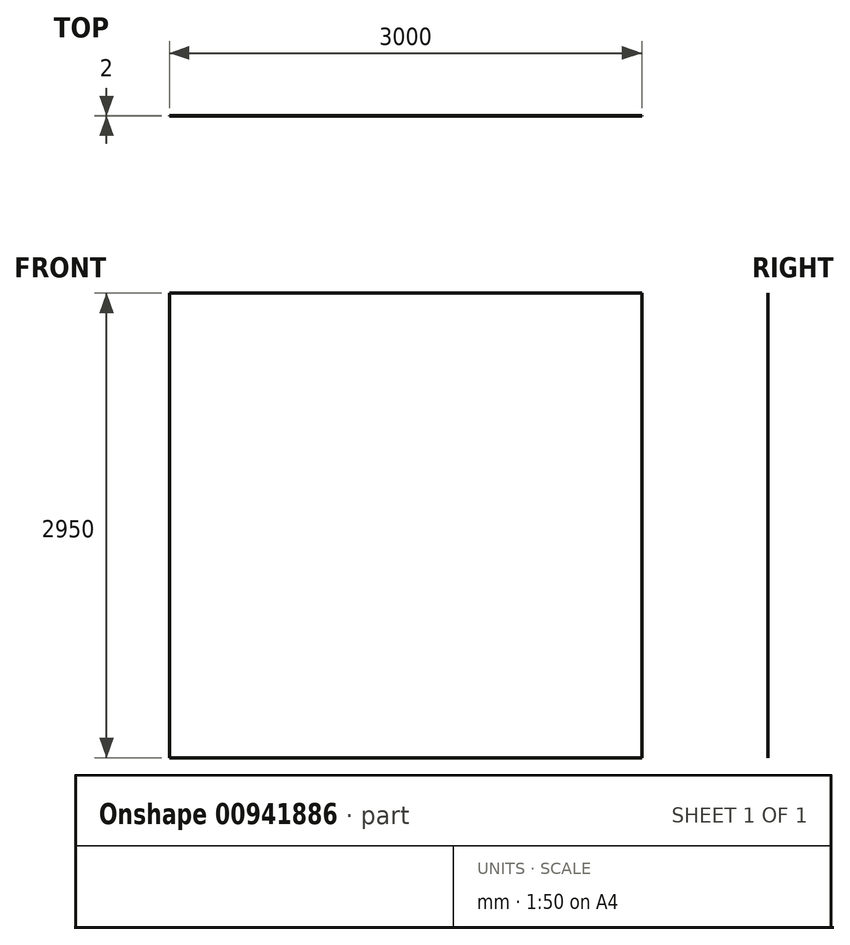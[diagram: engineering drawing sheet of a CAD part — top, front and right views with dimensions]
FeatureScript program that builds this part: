
annotation { "Feature Type Name" : "Feature", "Feature Type Description" : "" }
export const myFeature = defineFeature(function(context is Context, id is Id, definition is map)
    precondition{}
    {
        {
            var Q0;
            Q0=qCreatedBy(makeId("Front.planeOp"),FACE);
            var sketch = newSketch(context, id + "F0", { "sketchPlane" : qUnion([Q0])});
            skLineSegment(sketch, "E0.bottom", {"start": v(0, 0) * mm, "end": v(3000, 0) * mm});
            skLineSegment(sketch, "E0.top", {"start": v(0, -2950) * mm, "end": v(3000, -2950) * mm});
            skLineSegment(sketch, "E0.left", {"start": v(0, 0) * mm, "end": v(0, -2950) * mm});
            skLineSegment(sketch, "E0.right", {"start": v(3000, 0) * mm, "end": v(3000, -2950) * mm});
            skSolve(sketch);
        }
        {
            var Q0;
            Q0=makeQuery(id+"F0.imprint","IMPRINT",FACE,{"disambiguationData":[TD([[makeQuery(id+"F0.imprint","IMPRINT",EDGE,{"derivedFrom":sQuery(id+"F0.wireOp",EDGE,"E0.bottom")}),-1.0]])]});
            extrude(context, id + "F1", {"entities" : qUnion([Q0]), "depth" : 2 * mm, "offsetDistance" : 25 * mm});
        }
    });
